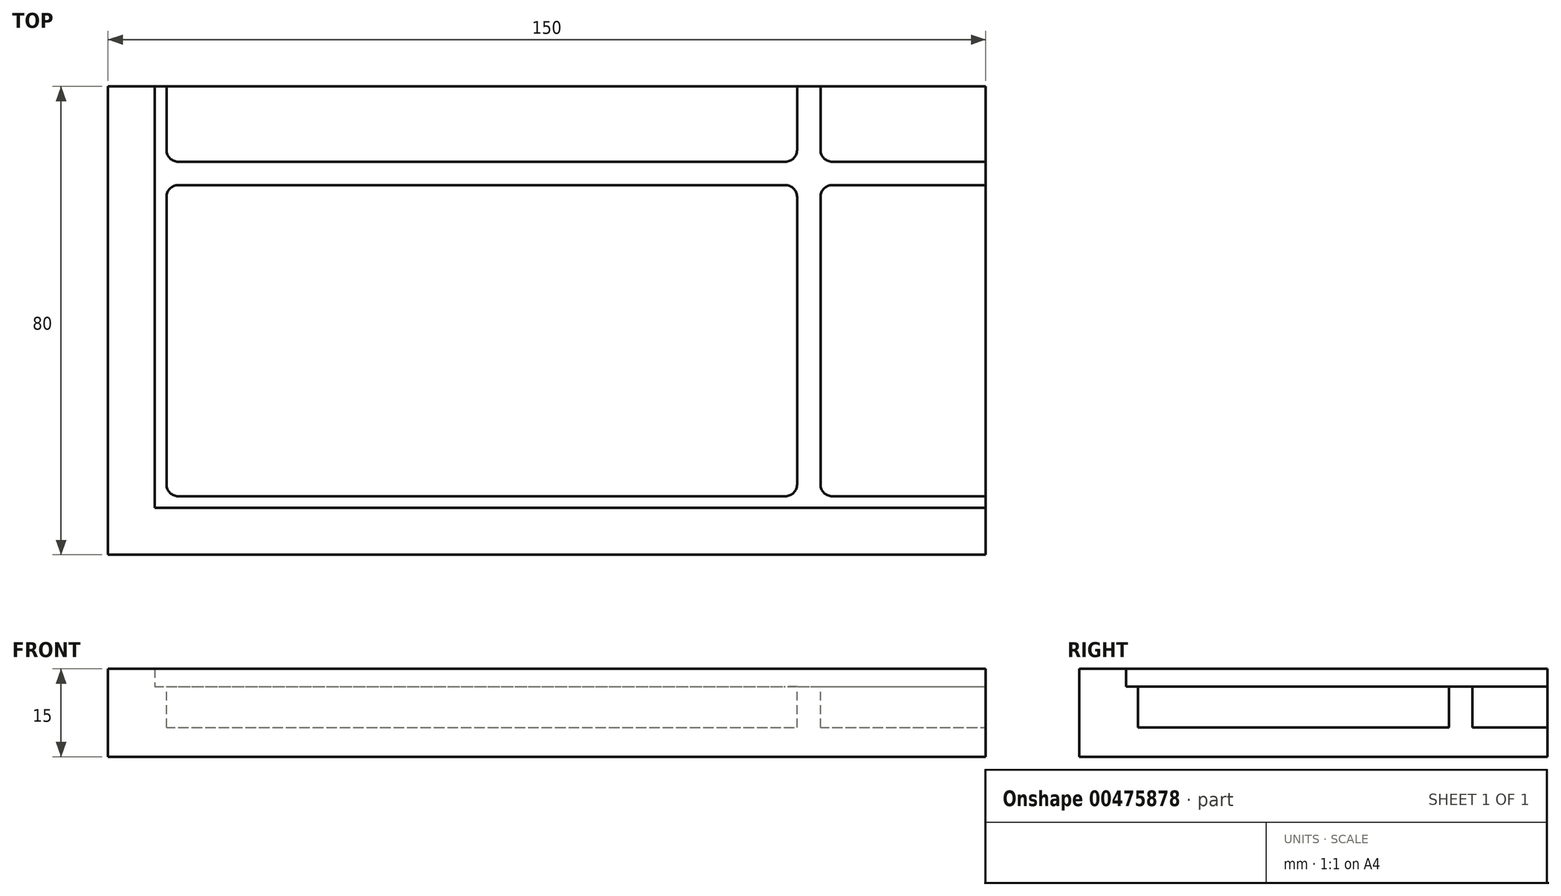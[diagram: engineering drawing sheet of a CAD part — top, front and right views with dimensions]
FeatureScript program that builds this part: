
annotation { "Feature Type Name" : "Feature", "Feature Type Description" : "" }
export const myFeature = defineFeature(function(context is Context, id is Id, definition is map)
    precondition{}
    {
        {
            var Q0;
            Q0=qCreatedBy(makeId("Top.planeOp"),FACE);
            var sketch = newSketch(context, id + "F0", { "sketchPlane" : qUnion([Q0])});
            skLineSegment(sketch, "E0.bottom", {"start": v(0, 0) * mm, "end": v(150, 0) * mm});
            skLineSegment(sketch, "E0.top", {"start": v(0, 80) * mm, "end": v(150, 80) * mm});
            skLineSegment(sketch, "E0.left", {"start": v(0, 0) * mm, "end": v(0, 80) * mm});
            skLineSegment(sketch, "E0.right", {"start": v(150, 0) * mm, "end": v(150, 80) * mm});
            skSolve(sketch);
        }
        {
            var Q0;
            Q0=makeQuery(id+"F0.imprint","IMPRINT",FACE,{"disambiguationData":[TD([[makeQuery(id+"F0.imprint","IMPRINT",EDGE,{"derivedFrom":sQuery(id+"F0.wireOp",EDGE,"E0.bottom")}),1.0]])]});
            extrude(context, id + "F1", {"entities" : qUnion([Q0]), "depth" : 12 * mm});
        }
        {
            var Q0;
            Q0=makeQuery(id+"F1.opExtrude","CAP_FACE",FACE,{"disambiguationData":[OSD([sQuery(id+"F0.wireOp",EDGE,"E0.bottom"),sQuery(id+"F0.wireOp",EDGE,"E0.top"),sQuery(id+"F0.wireOp",EDGE,"E0.left"),sQuery(id+"F0.wireOp",EDGE,"E0.right")])],"isStart":false});
            var sketch = newSketch(context, id + "F2", { "sketchPlane" : qUnion([Q0])});
            skLineSegment(sketch, "E1.bottom", {"start": v(0, 0) * mm, "end": v(8, 0) * mm});
            skLineSegment(sketch, "E1.top", {"start": v(0, 80) * mm, "end": v(8, 80) * mm});
            skLineSegment(sketch, "E1.left", {"start": v(0, 0) * mm, "end": v(0, 80) * mm});
            skLineSegment(sketch, "E1.right", {"start": v(8, 0) * mm, "end": v(8, 80) * mm});
            skLineSegment(sketch, "E2.bottom", {"start": v(8, 0) * mm, "end": v(150, 0) * mm});
            skLineSegment(sketch, "E2.top", {"start": v(8, 8) * mm, "end": v(150, 8) * mm});
            skLineSegment(sketch, "E2.left", {"start": v(8, 0) * mm, "end": v(8, 8) * mm});
            skLineSegment(sketch, "E2.right", {"start": v(150, 0) * mm, "end": v(150, 8) * mm});
            skSolve(sketch);
        }
        {
            var Q0;
            Q0=makeQuery(id+"F2.imprint","IMPRINT",FACE,{"disambiguationData":[TD([[makeQuery(id+"F2.imprint","IMPRINT",EDGE,{"derivedFrom":sQuery(id+"F2.wireOp",EDGE,"E1.bottom")}),1.0]])]});
            var Q1;
            Q1=makeQuery(id+"F2.imprint","IMPRINT",FACE,{"disambiguationData":[TD([[makeQuery(id+"F2.imprint","IMPRINT",EDGE,{"derivedFrom":sQuery(id+"F2.wireOp",EDGE,"E2.bottom")}),1.0]])]});
            extrude(context, id + "F3", {"entities" : qUnion([Q0, Q1]), "operationType" : NewBodyOperationType.ADD, "depth" : 3 * mm});
        }
        {
            var Q0;
            Q0=makeQuery(id+"F1.opExtrude","CAP_FACE",FACE,{"disambiguationData":[OSD([sQuery(id+"F0.wireOp",EDGE,"E0.bottom"),sQuery(id+"F0.wireOp",EDGE,"E0.top"),sQuery(id+"F0.wireOp",EDGE,"E0.left"),sQuery(id+"F0.wireOp",EDGE,"E0.right")])],"isStart":false});
            var sketch = newSketch(context, id + "F4", { "sketchPlane" : qUnion([Q0])});
            skLineSegment(sketch, "E3.bottom", {"start": v(8, 8) * mm, "end": v(119.76, 8) * mm, "construction": true});
            skLineSegment(sketch, "E3.top", {"start": v(8, 65.15) * mm, "end": v(119.76, 65.15) * mm, "construction": true});
            skLineSegment(sketch, "E3.left", {"start": v(8, 8) * mm, "end": v(8, 65.15) * mm, "construction": true});
            skLineSegment(sketch, "E3.right", {"start": v(119.76, 8) * mm, "end": v(119.76, 65.15) * mm, "construction": true});
            skLineSegment(sketch, "E4.bottom", {"start": v(8, 8) * mm, "end": v(150, 8) * mm});
            skLineSegment(sketch, "E4.top", {"start": v(8, 10) * mm, "end": v(150, 10) * mm});
            skLineSegment(sketch, "E4.left", {"start": v(8, 8) * mm, "end": v(8, 10) * mm});
            skLineSegment(sketch, "E4.right", {"start": v(150, 8) * mm, "end": v(150, 10) * mm});
            skLineSegment(sketch, "E5.bottom", {"start": v(8, 10) * mm, "end": v(10, 10) * mm});
            skLineSegment(sketch, "E5.top", {"start": v(8, 80) * mm, "end": v(10, 80) * mm});
            skLineSegment(sketch, "E5.left", {"start": v(8, 10) * mm, "end": v(8, 80) * mm});
            skLineSegment(sketch, "E5.right", {"start": v(10, 10) * mm, "end": v(10, 80) * mm});
            skLineSegment(sketch, "E6.bottom", {"start": v(8, 65.15) * mm, "end": v(150, 65.15) * mm});
            skLineSegment(sketch, "E6.top", {"start": v(8, 63.15) * mm, "end": v(150, 63.15) * mm});
            skLineSegment(sketch, "E6.left", {"start": v(8, 65.15) * mm, "end": v(8, 63.15) * mm});
            skLineSegment(sketch, "E6.right", {"start": v(150, 65.15) * mm, "end": v(150, 63.15) * mm});
            skLineSegment(sketch, "E7.bottom", {"start": v(119.76, 8) * mm, "end": v(117.76, 8) * mm});
            skLineSegment(sketch, "E7.top", {"start": v(119.76, 80) * mm, "end": v(117.76, 80) * mm});
            skLineSegment(sketch, "E7.left", {"start": v(119.76, 8) * mm, "end": v(119.76, 80) * mm});
            skLineSegment(sketch, "E7.right", {"start": v(117.76, 8) * mm, "end": v(117.76, 80) * mm});
            skLineSegment(sketch, "E8.top", {"start": v(8, 67.15) * mm, "end": v(150, 67.15) * mm});
            skLineSegment(sketch, "E8.left", {"start": v(8, 65.15) * mm, "end": v(8, 67.15) * mm});
            skLineSegment(sketch, "E8.right", {"start": v(150, 65.15) * mm, "end": v(150, 67.15) * mm});
            skLineSegment(sketch, "E9.bottom", {"start": v(119.76, 8) * mm, "end": v(121.76, 8) * mm});
            skLineSegment(sketch, "E9.top", {"start": v(119.76, 80) * mm, "end": v(121.76, 80) * mm});
            skLineSegment(sketch, "E9.right", {"start": v(121.76, 8) * mm, "end": v(121.76, 80) * mm});
            skSolve(sketch);
        }
        {
            var Q0;
            {var subQ0=sQuery(id+"F4.wireOp",EDGE,"E5.right");var subQ3=sQuery(id+"F4.wireOp",EDGE,"E8.top");var subQ4=makeQuery(id+"F4.imprint","INTERSECT",VERTEX,{"derivedFrom":[subQ0,subQ3]});Q0=makeQuery(id+"F4.imprint","IMPRINT",FACE,{"disambiguationData":[TD([[makeQuery(id+"F4.imprint","IMPRINT",EDGE,{"disambiguationData":[TD([[subQ4,-1.0]])],"derivedFrom":subQ3}),1.0]])]});}
            var Q1;
            {var subQ0=sQuery(id+"F4.wireOp",EDGE,"E5.right");var subQ5=sQuery(id+"F4.wireOp",EDGE,"E6.top");var subQ6=makeQuery(id+"F4.imprint","INTERSECT",VERTEX,{"derivedFrom":[subQ0,subQ5]});Q1=makeQuery(id+"F4.imprint","IMPRINT",FACE,{"disambiguationData":[TD([[makeQuery(id+"F4.imprint","IMPRINT",EDGE,{"disambiguationData":[TD([[subQ6,-1.0]])],"derivedFrom":subQ5}),-1.0]])]});}
            var Q2;
            {var subQ0=sQuery(id+"F4.wireOp",EDGE,"E4.top");var subQ3=sQuery(id+"F4.wireOp",EDGE,"E9.right");var subQ4=makeQuery(id+"F4.imprint","INTERSECT",VERTEX,{"derivedFrom":[subQ0,subQ3]});Q2=makeQuery(id+"F4.imprint","IMPRINT",FACE,{"disambiguationData":[TD([[makeQuery(id+"F4.imprint","IMPRINT",EDGE,{"disambiguationData":[TD([[subQ4,-1.0]])],"derivedFrom":subQ3}),-1.0]])]});}
            var Q3;
            {var subQ0=sQuery(id+"F4.wireOp",EDGE,"E8.top");var subQ3=sQuery(id+"F4.wireOp",EDGE,"E9.right");var subQ4=makeQuery(id+"F4.imprint","INTERSECT",VERTEX,{"derivedFrom":[subQ0,subQ3]});Q3=makeQuery(id+"F4.imprint","IMPRINT",FACE,{"disambiguationData":[TD([[makeQuery(id+"F4.imprint","IMPRINT",EDGE,{"disambiguationData":[TD([[subQ4,-1.0]])],"derivedFrom":subQ0}),1.0]])]});}
            extrude(context, id + "F5", {"entities" : qUnion([Q0, Q1, Q2, Q3]), "operationType" : NewBodyOperationType.REMOVE, "oppositeDirection" : true, "depth" : 7 * mm});
        }
        {
            var Q0;
            Q0=makeQuery(id+"F5.boolean.opBoolean","COPY",EDGE,{"derivedFrom":makeQuery(id+"F5.opExtrude","SWEPT_EDGE",EDGE,{"disambiguationData":[OSD([sQuery(id+"F4.wireOp",EDGE,"E5.right"),sQuery(id+"F4.wireOp",EDGE,"E6.top")])]})});
            var Q1;
            Q1=makeQuery(id+"F5.boolean.opBoolean","COPY",EDGE,{"derivedFrom":makeQuery(id+"F5.opExtrude","SWEPT_EDGE",EDGE,{"disambiguationData":[OSD([sQuery(id+"F4.wireOp",EDGE,"E6.top"),sQuery(id+"F4.wireOp",EDGE,"E7.right")])]})});
            var Q2;
            Q2=makeQuery(id+"F5.boolean.opBoolean","COPY",EDGE,{"derivedFrom":makeQuery(id+"F5.opExtrude","SWEPT_EDGE",EDGE,{"disambiguationData":[OSD([sQuery(id+"F4.wireOp",EDGE,"E6.top"),sQuery(id+"F4.wireOp",EDGE,"E9.right")])]})});
            var Q3;
            Q3=makeQuery(id+"F5.boolean.opBoolean","COPY",EDGE,{"derivedFrom":makeQuery(id+"F5.opExtrude","SWEPT_EDGE",EDGE,{"disambiguationData":[OSD([sQuery(id+"F4.wireOp",EDGE,"E8.top"),sQuery(id+"F4.wireOp",EDGE,"E9.right")])]})});
            var Q4;
            Q4=makeQuery(id+"F5.boolean.opBoolean","COPY",EDGE,{"derivedFrom":makeQuery(id+"F5.opExtrude","SWEPT_EDGE",EDGE,{"disambiguationData":[OSD([sQuery(id+"F4.wireOp",EDGE,"E7.right"),sQuery(id+"F4.wireOp",EDGE,"E8.top")])]})});
            var Q5;
            Q5=makeQuery(id+"F5.boolean.opBoolean","COPY",EDGE,{"derivedFrom":makeQuery(id+"F5.opExtrude","SWEPT_EDGE",EDGE,{"disambiguationData":[OSD([sQuery(id+"F4.wireOp",EDGE,"E4.top"),sQuery(id+"F4.wireOp",EDGE,"E7.right")])]})});
            var Q6;
            Q6=makeQuery(id+"F5.boolean.opBoolean","COPY",EDGE,{"derivedFrom":makeQuery(id+"F5.opExtrude","SWEPT_EDGE",EDGE,{"disambiguationData":[OSD([sQuery(id+"F4.wireOp",EDGE,"E4.top"),sQuery(id+"F4.wireOp",EDGE,"E5.bottom"),sQuery(id+"F4.wireOp",EDGE,"E5.right")])]})});
            var Q7;
            Q7=makeQuery(id+"F5.boolean.opBoolean","COPY",EDGE,{"derivedFrom":makeQuery(id+"F5.opExtrude","SWEPT_EDGE",EDGE,{"disambiguationData":[OSD([sQuery(id+"F4.wireOp",EDGE,"E5.right"),sQuery(id+"F4.wireOp",EDGE,"E8.top")])]})});
            var Q8;
            Q8=makeQuery(id+"F5.boolean.opBoolean","COPY",EDGE,{"derivedFrom":makeQuery(id+"F5.opExtrude","SWEPT_EDGE",EDGE,{"disambiguationData":[OSD([sQuery(id+"F4.wireOp",EDGE,"E4.top"),sQuery(id+"F4.wireOp",EDGE,"E9.right")])]})});
            fillet(context, id + "F6", {"entities" : qUnion([Q0, Q1, Q2, Q3, Q4, Q5, Q6, Q7, Q8]), "radius" : 2 * mm, "tangentPropagation" : true, "allowEdgeOverflow" : false});
        }
    });
